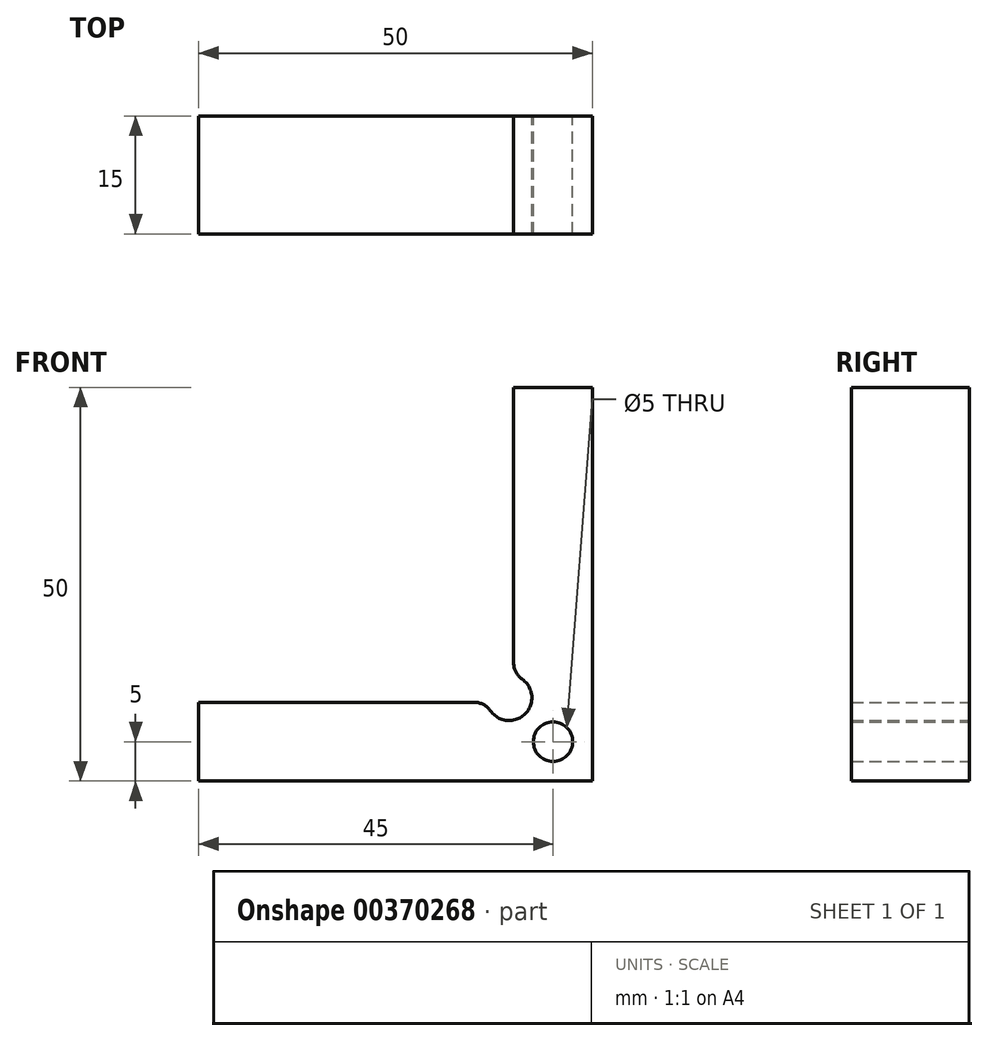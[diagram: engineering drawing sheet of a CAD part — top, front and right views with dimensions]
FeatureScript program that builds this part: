
annotation { "Feature Type Name" : "Feature", "Feature Type Description" : "" }
export const myFeature = defineFeature(function(context is Context, id is Id, definition is map)
    precondition{}
    {
        {
            var Q0;
            Q0=qCreatedBy(makeId("Front.planeOp"),FACE);
            var sketch = newSketch(context, id + "F0", { "sketchPlane" : qUnion([Q0])});
            skLineSegment(sketch, "E0", {"start": v(-5, 45) * mm, "end": v(-5, 5) * mm});
            skLineSegment(sketch, "E1", {"start": v(-5, 5) * mm, "end": v(-45, 5) * mm});
            skLineSegment(sketch, "E2", {"start": v(-45, 5) * mm, "end": v(-45, -5) * mm});
            skLineSegment(sketch, "E3", {"start": v(-45, -5) * mm, "end": v(5, -5) * mm});
            skLineSegment(sketch, "E4", {"start": v(5, -5) * mm, "end": v(5, 45) * mm});
            skLineSegment(sketch, "E5", {"start": v(5, 45) * mm, "end": v(-5, 45) * mm});
            skCircle(sketch, "E6", {"center": v(0, 0) * mm, "radius": 2.5 * mm});
            skSolve(sketch);
        }
        {
            var Q0;
            Q0=makeQuery(id+"F0.imprint","IMPRINT",FACE,{"disambiguationData":[TD([[makeQuery(id+"F0.imprint","IMPRINT",EDGE,{"derivedFrom":sQuery(id+"F0.wireOp",EDGE,"E0")}),1.0]])]});
            extrude(context, id + "F1", {"entities" : qUnion([Q0]), "depth" : 15 * mm});
        }
        {
            var Q0;
            Q0=makeQuery(id+"F1.opExtrude","SWEPT_EDGE",EDGE,{"disambiguationData":[OSD([sQuery(id+"F0.wireOp",EDGE,"E0"),sQuery(id+"F0.wireOp",EDGE,"E1")])]});
            fillet(context, id + "F2", {"entities" : qUnion([Q0]), "radius" : 5 * mm, "tangentPropagation" : true, "allowEdgeOverflow" : false});
        }
        {
            var Q0;
            Q0=qCreatedBy(makeId("Front.planeOp"),FACE);
            var sketch = newSketch(context, id + "F3", { "sketchPlane" : qUnion([Q0])});
            skArc(sketch, "E7", {"start": v(-7.95, 3.93) * mm, "mid": v(-8.84, 4.72) * mm, "end": v(-10, 5) * mm});
            skArc(sketch, "E8", {"start": v(-5, 10) * mm, "mid": v(-4.72, 8.84) * mm, "end": v(-3.93, 7.95) * mm});
            skArc(sketch, "E9", {"start": v(-7.95, 3.93) * mm, "mid": v(-3.54, 3.54) * mm, "end": v(-3.93, 7.95) * mm});
            skArc(sketch, "E10", {"start": v(-10, 5) * mm, "mid": v(-6.46, 6.46) * mm, "end": v(-5, 10) * mm});
            skSolve(sketch);
        }
        {
            var Q0;
            Q0 = qSketchRegion(id + "F3", true);
            extrude(context, id + "F4", {"entities" : qUnion([Q0]), "operationType" : NewBodyOperationType.REMOVE, "depth" : 25 * mm});
        }
    });
